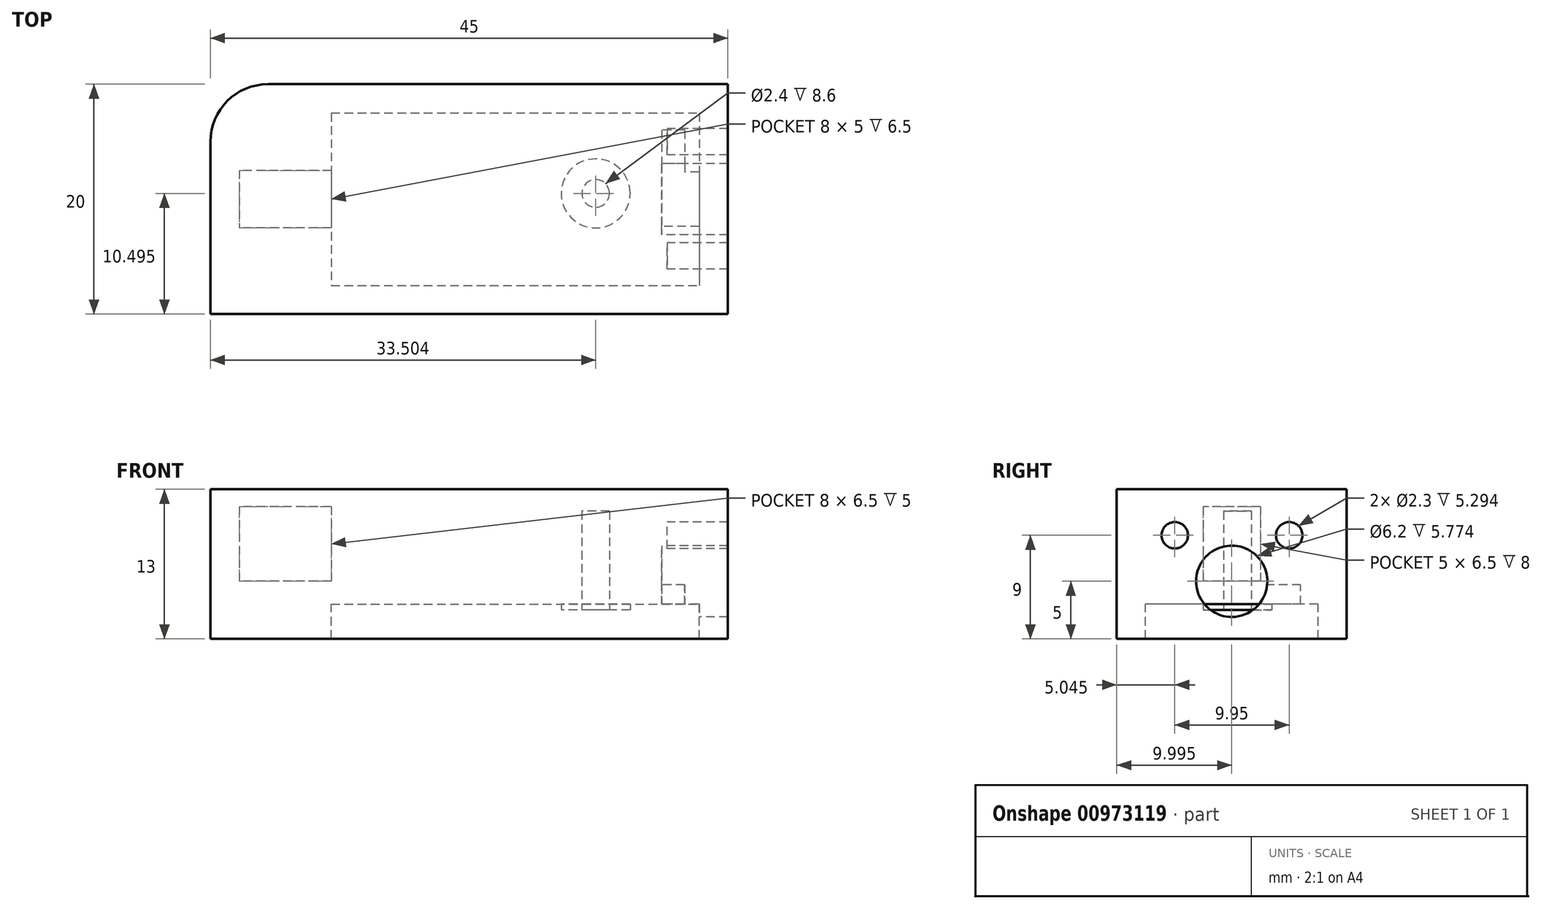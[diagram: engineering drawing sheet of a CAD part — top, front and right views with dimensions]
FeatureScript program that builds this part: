
annotation { "Feature Type Name" : "Feature", "Feature Type Description" : "" }
export const myFeature = defineFeature(function(context is Context, id is Id, definition is map)
    precondition{}
    {
        {
            var Q0;
            Q0=qCreatedBy(makeId("Top.planeOp"),FACE);
            var sketch = newSketch(context, id + "F0", { "sketchPlane" : qUnion([Q0])});
            skLineSegment(sketch, "E0.bottom", {"start": v(-23, 39.55) * mm, "end": v(22, 39.55) * mm});
            skLineSegment(sketch, "E0.top", {"start": v(-23, 19.55) * mm, "end": v(22, 19.55) * mm});
            skLineSegment(sketch, "E0.left", {"start": v(-23, 39.55) * mm, "end": v(-23, 19.55) * mm});
            skLineSegment(sketch, "E0.right", {"start": v(22, 39.55) * mm, "end": v(22, 19.55) * mm});
            skLineSegment(sketch, "E1.bottom", {"start": v(-9.93, 19.55) * mm, "end": v(10.07, 19.55) * mm});
            skLineSegment(sketch, "E1.top", {"start": v(-9.93, -0.45) * mm, "end": v(10.07, -0.45) * mm});
            skLineSegment(sketch, "E1.left", {"start": v(-9.93, 19.55) * mm, "end": v(-9.93, -0.45) * mm});
            skLineSegment(sketch, "E1.right", {"start": v(10.07, 19.55) * mm, "end": v(10.07, -0.45) * mm});
            skLineSegment(sketch, "E2", {"start": v(-9.93, 4.55) * mm, "end": v(10.07, 4.55) * mm});
            skLineSegment(sketch, "E3.bottom", {"start": v(-12.5, 37.05) * mm, "end": v(19.5, 37.05) * mm});
            skLineSegment(sketch, "E3.top", {"start": v(-12.5, 22.05) * mm, "end": v(19.5, 22.05) * mm});
            skLineSegment(sketch, "E3.left", {"start": v(-12.5, 37.05) * mm, "end": v(-12.5, 22.05) * mm});
            skLineSegment(sketch, "E3.right", {"start": v(19.5, 37.05) * mm, "end": v(19.5, 22.05) * mm});
            skLineSegment(sketch, "E4.bottom", {"start": v(-12.5, 32.05) * mm, "end": v(-20.5, 32.05) * mm});
            skLineSegment(sketch, "E4.top", {"start": v(-12.5, 27.05) * mm, "end": v(-20.5, 27.05) * mm});
            skLineSegment(sketch, "E4.left", {"start": v(-12.5, 32.05) * mm, "end": v(-12.5, 27.05) * mm});
            skLineSegment(sketch, "E4.right", {"start": v(-20.5, 32.05) * mm, "end": v(-20.5, 27.05) * mm});
            skLineSegment(sketch, "E5", {"start": v(-16.5, 32.05) * mm, "end": v(-16.5, 27.05) * mm});
            skCircle(sketch, "E6", {"center": v(10.5, 30.05) * mm, "radius": 3 * mm});
            skCircle(sketch, "E7", {"center": v(10.5, 30.05) * mm, "radius": 1.2 * mm});
            skLineSegment(sketch, "E8.bottom", {"start": v(18.24, 35.55) * mm, "end": v(16.24, 35.55) * mm});
            skLineSegment(sketch, "E8.top", {"start": v(18.24, 27.55) * mm, "end": v(16.24, 27.55) * mm});
            skLineSegment(sketch, "E8.left", {"start": v(18.24, 35.55) * mm, "end": v(18.24, 27.55) * mm});
            skLineSegment(sketch, "E8.right", {"start": v(16.24, 35.55) * mm, "end": v(16.24, 27.55) * mm});
            skSolve(sketch);
        }
        {
            var Q0;
            Q0=makeQuery(id+"F0.imprint","IMPRINT",FACE,{"disambiguationData":[TD([[makeQuery(id+"F0.imprint","IMPRINT",EDGE,{"derivedFrom":sQuery(id+"F0.wireOp",EDGE,"E0.bottom")}),-1.0]])]});
            var Q1;
            {var subQ0=sQuery(id+"F0.wireOp",EDGE,"E4.right");Q1=makeQuery(id+"F0.imprint","IMPRINT",FACE,{"disambiguationData":[TD([[makeQuery(id+"F0.imprint","IMPRINT",EDGE,{"derivedFrom":subQ0}),1.0]])]});}
            var Q2;
            {var subQ5=sQuery(id+"F0.wireOp",EDGE,"E5");Q2=makeQuery(id+"F0.imprint","IMPRINT",FACE,{"disambiguationData":[TD([[makeQuery(id+"F0.imprint","IMPRINT",EDGE,{"derivedFrom":subQ5}),1.0]])]});}
            var Q3;
            {var subQ3=sQuery(id+"F0.wireOp",EDGE,"E3.bottom");Q3=makeQuery(id+"F0.imprint","IMPRINT",FACE,{"disambiguationData":[TD([[makeQuery(id+"F0.imprint","IMPRINT",EDGE,{"derivedFrom":subQ3}),-1.0]])]});}
            var Q4;
            Q4=makeQuery(id+"F0.imprint","IMPRINT",FACE,{"disambiguationData":[TD([[makeQuery(id+"F0.imprint","IMPRINT",EDGE,{"derivedFrom":sQuery(id+"F0.wireOp",EDGE,"E6")}),1.0]])]});
            var Q5;
            Q5=makeQuery(id+"F0.imprint","IMPRINT",FACE,{"disambiguationData":[TD([[makeQuery(id+"F0.imprint","IMPRINT",EDGE,{"derivedFrom":sQuery(id+"F0.wireOp",EDGE,"E7")}),1.0]])]});
            var Q6;
            Q6=makeQuery(id+"F0.imprint","IMPRINT",FACE,{"disambiguationData":[TD([[makeQuery(id+"F0.imprint","IMPRINT",EDGE,{"derivedFrom":sQuery(id+"F0.wireOp",EDGE,"E8.bottom")}),1.0]])]});
            extrude(context, id + "F1", {"entities" : qUnion([Q0, Q1, Q2, Q3, Q4, Q5, Q6]), "depth" : 10 * mm, "offsetDistance" : 25 * mm});
        }
        {
            var Q0;
            Q0=makeQuery(id+"F0.imprint","IMPRINT",FACE,{"disambiguationData":[TD([[makeQuery(id+"F0.imprint","IMPRINT",EDGE,{"derivedFrom":sQuery(id+"F0.wireOp",EDGE,"E0.bottom")}),-1.0]])]});
            var Q1;
            {var subQ5=sQuery(id+"F0.wireOp",EDGE,"E5");Q1=makeQuery(id+"F0.imprint","IMPRINT",FACE,{"disambiguationData":[TD([[makeQuery(id+"F0.imprint","IMPRINT",EDGE,{"derivedFrom":subQ5}),1.0]])]});}
            var Q2;
            {var subQ0=sQuery(id+"F0.wireOp",EDGE,"E4.right");Q2=makeQuery(id+"F0.imprint","IMPRINT",FACE,{"disambiguationData":[TD([[makeQuery(id+"F0.imprint","IMPRINT",EDGE,{"derivedFrom":subQ0}),1.0]])]});}
            extrude(context, id + "F2", {"entities" : qUnion([Q0, Q1, Q2]), "operationType" : NewBodyOperationType.ADD, "oppositeDirection" : true, "depth" : 3 * mm, "offsetDistance" : 25 * mm});
        }
        {
            var Q0;
            {var subQ0=sQuery(id+"F0.wireOp",EDGE,"E4.right");Q0=makeQuery(id+"F0.imprint","IMPRINT",FACE,{"disambiguationData":[TD([[makeQuery(id+"F0.imprint","IMPRINT",EDGE,{"derivedFrom":subQ0}),1.0]])]});}
            var Q1;
            Q1=makeQuery(id+"F1.opExtrude","CAP_FACE",FACE,{"disambiguationData":[OSD([sQuery(id+"F0.wireOp",EDGE,"E0.bottom"),sQuery(id+"F0.wireOp",EDGE,"E0.top"),sQuery(id+"F0.wireOp",EDGE,"E0.left"),sQuery(id+"F0.wireOp",EDGE,"E0.right")])],"isStart":false});
            var Q2;
            {var subQ5=sQuery(id+"F0.wireOp",EDGE,"E5");Q2=makeQuery(id+"F0.imprint","IMPRINT",FACE,{"disambiguationData":[TD([[makeQuery(id+"F0.imprint","IMPRINT",EDGE,{"derivedFrom":subQ5}),1.0]])]});}
            extrude(context, id + "F3", {"entities" : qUnion([Q0, Q1, Q2]), "operationType" : NewBodyOperationType.REMOVE, "depth" : 8.5 * mm, "offsetDistance" : 25 * mm, "hasSecondDirection" : true, "secondDirectionOppositeDirection" : false, "secondDirectionDepth" : 2 * mm});
        }
        {
            var Q0;
            Q0=makeQuery(id+"F0.imprint","IMPRINT",FACE,{"disambiguationData":[TD([[makeQuery(id+"F0.imprint","IMPRINT",EDGE,{"derivedFrom":sQuery(id+"F0.wireOp",EDGE,"E6")}),1.0]])]});
            extrude(context, id + "F4", {"entities" : qUnion([Q0]), "operationType" : NewBodyOperationType.ADD, "depth" : 6.5 * mm, "offsetDistance" : 25 * mm, "hasSecondDirection" : true, "secondDirectionOppositeDirection" : false, "secondDirectionDepth" : 5 * mm});
        }
        {
            var Q0;
            {var subQ0=sQuery(id+"F0.wireOp",EDGE,"E0.left");var subQ1=sQuery(id+"F0.wireOp",EDGE,"E0.bottom");Q0=makeQuery(id+"F2.boolean.opBoolean","MERGE",EDGE,{"derivedFrom":[makeQuery(id+"F1.opExtrude","SWEPT_EDGE",EDGE,{"disambiguationData":[OSD([subQ1,subQ0])]}),makeQuery(id+"F2.opExtrude","SWEPT_EDGE",EDGE,{"disambiguationData":[OSD([subQ1,subQ0])]})]});}
            fillet(context, id + "F5", {"entities" : qUnion([Q0]), "radius" : 5 * mm, "tangentPropagation" : true, "allowEdgeOverflow" : false});
        }
        {
            var Q0;
            Q0=makeQuery(id+"F0.imprint","IMPRINT",FACE,{"disambiguationData":[TD([[makeQuery(id+"F0.imprint","IMPRINT",EDGE,{"derivedFrom":sQuery(id+"F0.wireOp",EDGE,"E7")}),1.0]])]});
            extrude(context, id + "F6", {"entities" : qUnion([Q0]), "operationType" : NewBodyOperationType.REMOVE, "depth" : 8.1 * mm, "offsetDistance" : 25 * mm});
        }
        {
            var Q0;
            Q0=makeQuery(id+"F0.imprint","IMPRINT",FACE,{"disambiguationData":[TD([[makeQuery(id+"F0.imprint","IMPRINT",EDGE,{"derivedFrom":sQuery(id+"F0.wireOp",EDGE,"E6")}),1.0]])]});
            extrude(context, id + "F7", {"entities" : qUnion([Q0]), "operationType" : NewBodyOperationType.ADD, "depth" : 3 * mm, "offsetDistance" : 25 * mm, "hasSecondDirection" : true, "secondDirectionOppositeDirection" : true, "secondDirectionDepth" : .5 * mm});
        }
        {
            var Q0;
            Q0=makeQuery(id+"F0.imprint","IMPRINT",FACE,{"disambiguationData":[TD([[makeQuery(id+"F0.imprint","IMPRINT",EDGE,{"derivedFrom":sQuery(id+"F0.wireOp",EDGE,"E8.bottom")}),1.0]])]});
            extrude(context, id + "F8", {"entities" : qUnion([Q0]), "operationType" : NewBodyOperationType.REMOVE, "oppositeDirection" : true, "depth" : 25 * mm, "offsetDistance" : 25 * mm, "hasSecondDirection" : true, "secondDirectionOppositeDirection" : false, "secondDirectionDepth" : 1.7 * mm});
        }
        {
            var Q0;
            Q0=qCreatedBy(makeId("Right.planeOp"),FACE);
            var sketch = newSketch(context, id + "F9", { "sketchPlane" : qUnion([Q0])});
            skCircle(sketch, "E9", {"center": v(29.55, 2) * mm, "radius": 3.1 * mm});
            skCircle(sketch, "E10", {"center": v(34.55, 6) * mm, "radius": 1.15 * mm});
            skCircle(sketch, "E11", {"center": v(24.6, 6) * mm, "radius": 1.15 * mm});
            skSolve(sketch);
        }
        {
            var Q0;
            Q0=makeQuery(id+"F9.imprint","IMPRINT",FACE,{"disambiguationData":[TD([[makeQuery(id+"F9.imprint","IMPRINT",EDGE,{"derivedFrom":sQuery(id+"F9.wireOp",EDGE,"E9")}),1.0]])]});
            extrude(context, id + "F10", {"entities" : qUnion([Q0]), "operationType" : NewBodyOperationType.REMOVE, "depth" : 25.8 * mm, "offsetDistance" : 25 * mm, "hasSecondDirection" : true, "secondDirectionOppositeDirection" : false, "secondDirectionDepth" : 16.22 * mm});
        }
        {
            var Q0;
            Q0=makeQuery(id+"F9.imprint","IMPRINT",FACE,{"disambiguationData":[TD([[makeQuery(id+"F9.imprint","IMPRINT",EDGE,{"derivedFrom":sQuery(id+"F9.wireOp",EDGE,"E10")}),1.0]])]});
            var Q1;
            Q1=makeQuery(id+"F9.imprint","IMPRINT",FACE,{"disambiguationData":[TD([[makeQuery(id+"F9.imprint","IMPRINT",EDGE,{"derivedFrom":sQuery(id+"F9.wireOp",EDGE,"E11")}),1.0]])]});
            extrude(context, id + "F11", {"entities" : qUnion([Q0, Q1]), "operationType" : NewBodyOperationType.REMOVE, "depth" : 38.4 * mm, "offsetDistance" : 25 * mm, "hasSecondDirection" : true, "secondDirectionOppositeDirection" : false, "secondDirectionDepth" : 16.7 * mm});
        }
    });
